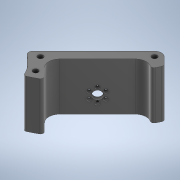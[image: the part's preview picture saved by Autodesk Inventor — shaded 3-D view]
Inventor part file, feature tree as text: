
AUTODESK INVENTOR PART (.ipt)
format: ipt  version: 2020 (Build 240168000, 168)  size: 475,648 bytes
history: native  units: mm
features: sketch x7, extrude x7, chamfer x2, projected_geometry x2, other x1, fillet x1
ambient origin geometry x8: Origin, YZ Plane, XZ Plane, XY Plane, X Axis, Y Axis, Z Axis, Center Point
bodies: Body1 (feature_tree)
feature tree (20):
  other  "Твердое тело1"
  sketch  "Эскиз1"
  extrude  "Выдавливание10"  Depth=3.8mm
  sketch  "Эскиз6"
  extrude  "Выдавливание13"  Depth=6.0mm
  extrude  "Выдавливание14"  Depth=35.0mm TaperAngle=0.0deg
  chamfer  "Фаска3"  Distance=59.0mm
  extrude  "Выдавливание15"  Depth=16.5mm
  fillet  "Сопряжение1"  Radius=10.0mm
  extrude  "Выдавливание16"  Depth=6.4mm
  extrude  "Выдавливание17"  Depth=2.3mm
  sketch  "Эскиз10"
  extrude  "Выдавливание18"  Depth=60.0mm TaperAngle=360.0deg
  chamfer  "Фаска4"  Distance=33.5mm
  sketch  "Эскиз7"
  sketch  "Эскиз8"
  projected_geometry  "Спроецированная петля3"
  sketch  "Эскиз9"
  projected_geometry  "Спроецированная петля4"
  sketch  "Эскиз11"
